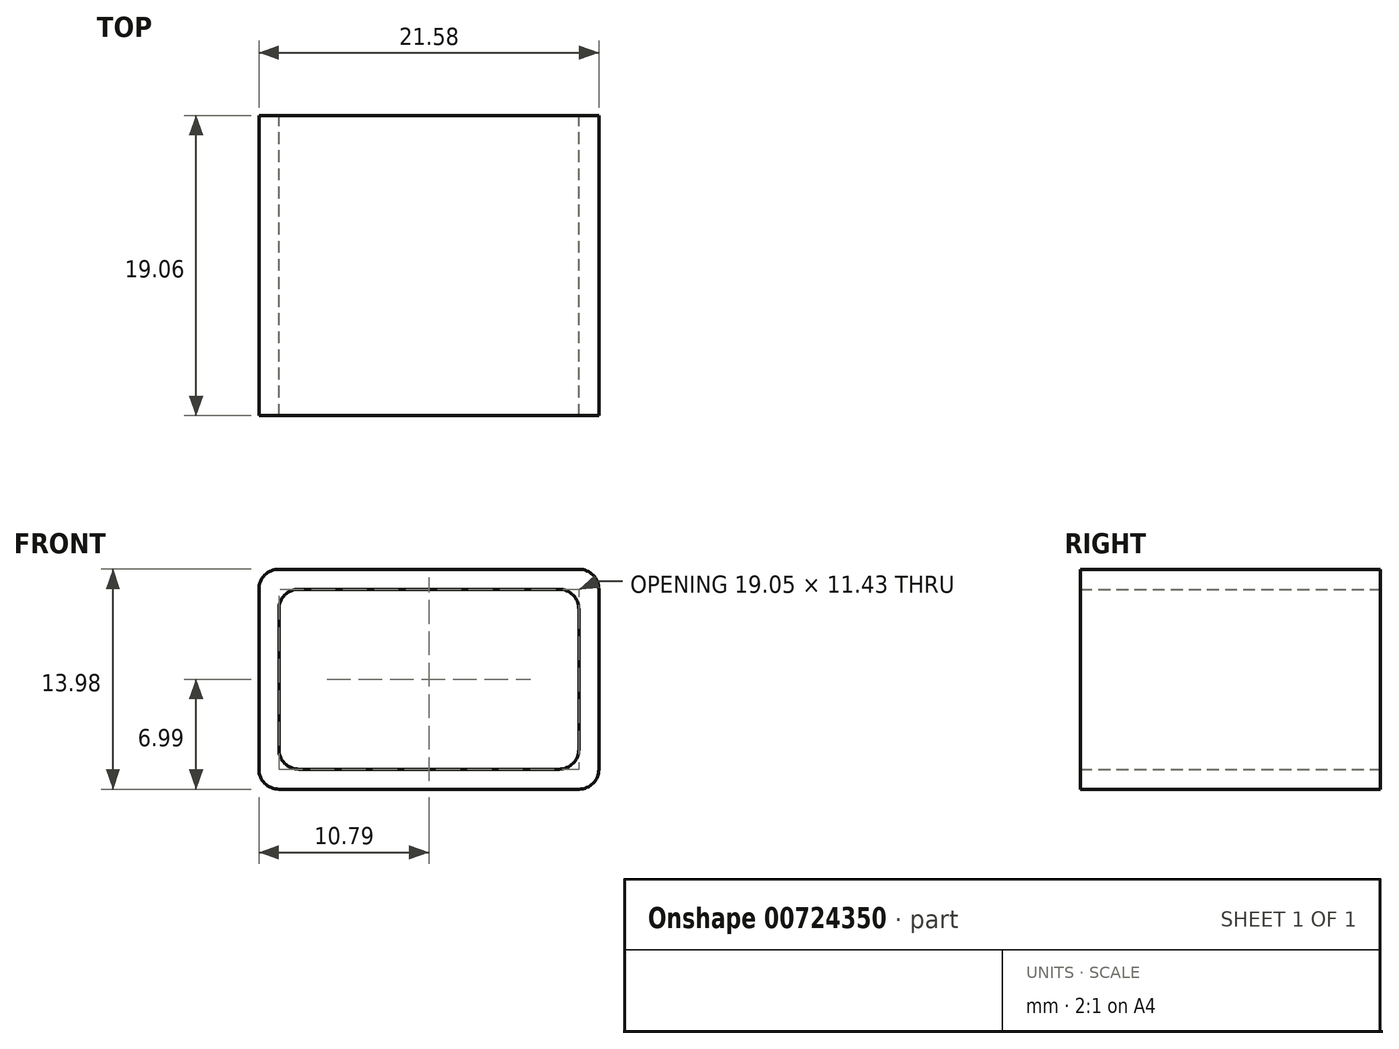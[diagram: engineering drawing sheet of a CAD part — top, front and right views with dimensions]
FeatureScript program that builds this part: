
annotation { "Feature Type Name" : "Feature", "Feature Type Description" : "" }
export const myFeature = defineFeature(function(context is Context, id is Id, definition is map)
    precondition{}
    {
        {
            var Q0;
            Q0=qCreatedBy(makeId("Front.planeOp"),FACE);
            var sketch = newSketch(context, id + "F0", { "sketchPlane" : qUnion([Q0])});
            skLineSegment(sketch, "E0.bottom", {"start": v(8.26, -5.72) * mm, "end": v(-8.26, -5.72) * mm});
            skLineSegment(sketch, "E0.top", {"start": v(8.26, 5.72) * mm, "end": v(-8.25, 5.72) * mm});
            skLineSegment(sketch, "E0.left", {"start": v(9.53, -4.45) * mm, "end": v(9.53, 4.45) * mm});
            skLineSegment(sketch, "E0.right", {"start": v(-9.53, -4.45) * mm, "end": v(-9.53, 4.45) * mm});
            skPoint(sketch, "E0.middle", {"position": v(0, 0) * mm});
            skLineSegment(sketch, "E1.bottom", {"start": v(9.53, -6.99) * mm, "end": v(-9.53, -6.99) * mm});
            skLineSegment(sketch, "E1.top", {"start": v(9.53, 6.99) * mm, "end": v(-9.53, 6.99) * mm});
            skLineSegment(sketch, "E1.left", {"start": v(10.8, -5.72) * mm, "end": v(10.8, 5.72) * mm});
            skLineSegment(sketch, "E1.right", {"start": v(-10.8, -5.72) * mm, "end": v(-10.8, 5.71) * mm});
            skPoint(sketch, "E2.visualSharp", {"position": v(-9.53, 5.72) * mm});
            skArc(sketch, "E2.filletArc", {"start": v(-8.25, 5.72) * mm, "mid": v(-9.15, 5.34) * mm, "end": v(-9.53, 4.45) * mm});
            skPoint(sketch, "E3.visualSharp", {"position": v(9.53, 5.72) * mm});
            skArc(sketch, "E3.filletArc", {"start": v(9.53, 4.45) * mm, "mid": v(9.15, 5.34) * mm, "end": v(8.26, 5.72) * mm});
            skPoint(sketch, "E4.visualSharp", {"position": v(-9.53, -5.72) * mm});
            skArc(sketch, "E4.filletArc", {"start": v(-9.53, -4.45) * mm, "mid": v(-9.15, -5.34) * mm, "end": v(-8.26, -5.72) * mm});
            skPoint(sketch, "E5.visualSharp", {"position": v(9.53, -5.72) * mm});
            skArc(sketch, "E5.filletArc", {"start": v(8.26, -5.72) * mm, "mid": v(9.15, -5.34) * mm, "end": v(9.52, -4.45) * mm});
            skPoint(sketch, "E6.visualSharp", {"position": v(10.8, -6.99) * mm});
            skArc(sketch, "E6.filletArc", {"start": v(9.53, -6.99) * mm, "mid": v(10.42, -6.61) * mm, "end": v(10.8, -5.72) * mm});
            skPoint(sketch, "E7.visualSharp", {"position": v(-10.8, -6.99) * mm});
            skArc(sketch, "E7.filletArc", {"start": v(-10.8, -5.72) * mm, "mid": v(-10.42, -6.61) * mm, "end": v(-9.53, -6.99) * mm});
            skPoint(sketch, "E8.visualSharp", {"position": v(-10.8, 6.99) * mm});
            skArc(sketch, "E8.filletArc", {"start": v(-9.53, 6.99) * mm, "mid": v(-10.42, 6.61) * mm, "end": v(-10.8, 5.71) * mm});
            skPoint(sketch, "E9.visualSharp", {"position": v(10.8, 6.99) * mm});
            skArc(sketch, "E9.filletArc", {"start": v(10.8, 5.72) * mm, "mid": v(10.42, 6.61) * mm, "end": v(9.53, 6.99) * mm});
            skSolve(sketch);
        }
        {
            var Q0;
            Q0 = qSketchRegion(id + "F0", true);
            extrude(context, id + "F1", {"entities" : qUnion([Q0]), "depth" : 9.52 * mm, "offsetDistance" : 25.4 * mm, "hasSecondDirection" : true, "secondDirectionOppositeDirection" : true, "secondDirectionDepth" : 9.52 * mm});
        }
    });
